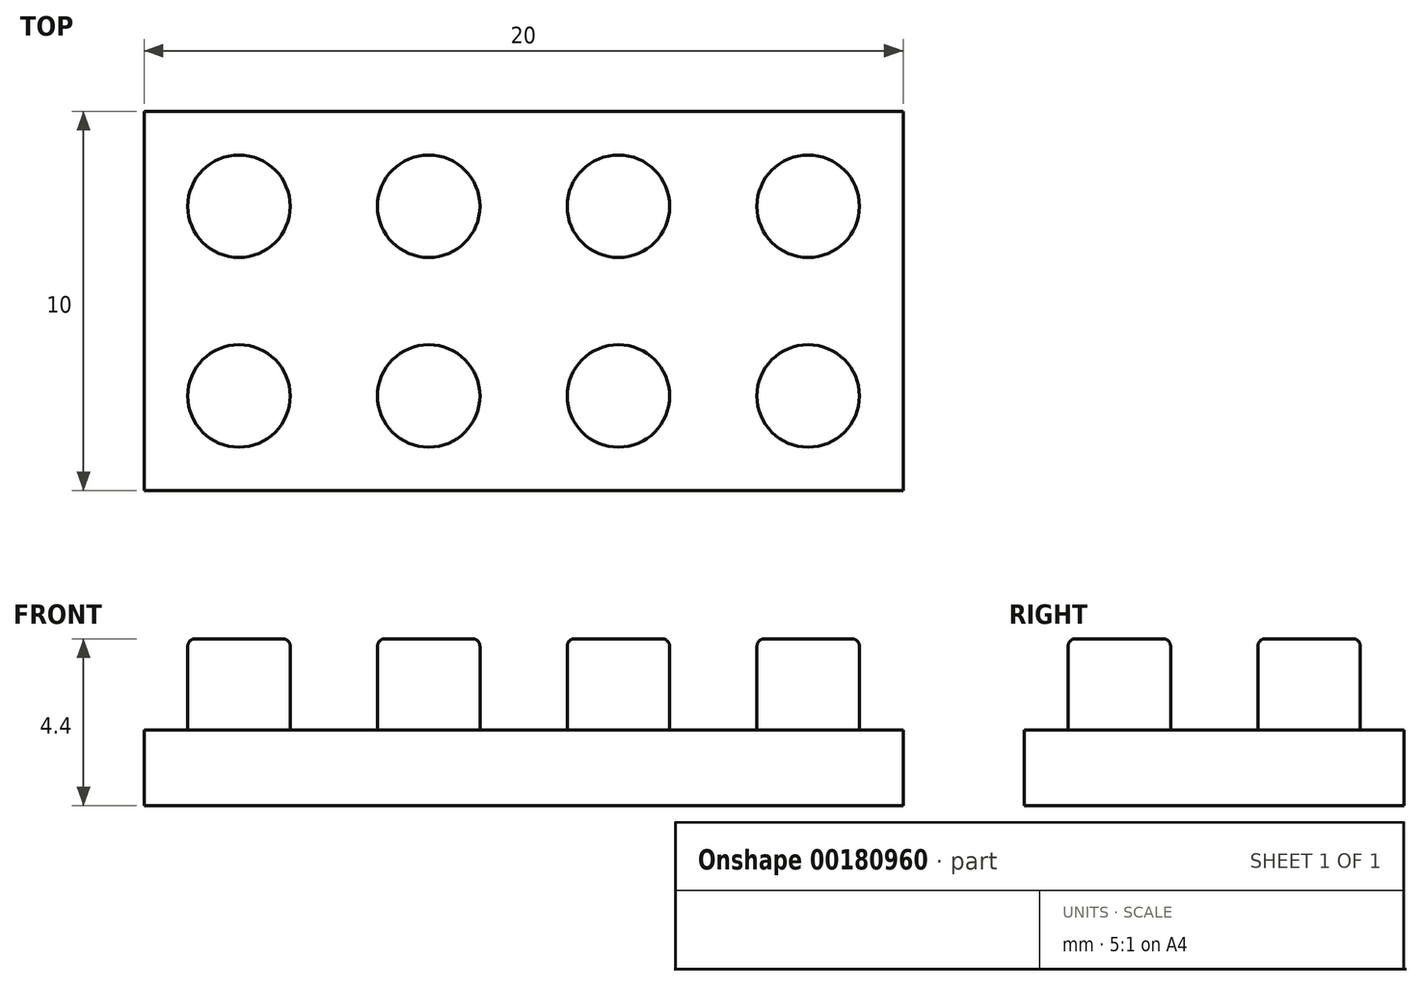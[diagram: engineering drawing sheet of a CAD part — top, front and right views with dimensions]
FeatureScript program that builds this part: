
annotation { "Feature Type Name" : "Feature", "Feature Type Description" : "" }
export const myFeature = defineFeature(function(context is Context, id is Id, definition is map)
    precondition{}
    {
        {
            var Q0;
            Q0=qCreatedBy(makeId("Top.planeOp"),FACE);
            var sketch = newSketch(context, id + "F0", { "sketchPlane" : qUnion([Q0])});
            skCircle(sketch, "E0", {"center": v(0, 0) * mm, "radius": 1.35 * mm});
            skCircle(sketch, "E1.0.1.0", {"center": v(0, 5) * mm, "radius": 1.35 * mm});
            skCircle(sketch, "E1.1.0.0", {"center": v(5, 0) * mm, "radius": 1.35 * mm});
            skCircle(sketch, "E1.1.1.0", {"center": v(5, 5) * mm, "radius": 1.35 * mm});
            skCircle(sketch, "E1.2.0.0", {"center": v(10, 0) * mm, "radius": 1.35 * mm});
            skCircle(sketch, "E1.2.1.0", {"center": v(10, 5) * mm, "radius": 1.35 * mm});
            skCircle(sketch, "E1.3.0.0", {"center": v(15, 0) * mm, "radius": 1.35 * mm});
            skCircle(sketch, "E1.3.1.0", {"center": v(15, 5) * mm, "radius": 1.35 * mm});
            skLineSegment(sketch, "E1.direction1", {"start": v(0, 0) * mm, "end": v(5, 0) * mm, "construction": true});
            skLineSegment(sketch, "E1.direction2", {"start": v(0, 0) * mm, "end": v(0, 5) * mm, "construction": true});
            skSolve(sketch);
        }
        {
            var Q0;
            Q0 = qSketchRegion(id + "F0", true);
            extrude(context, id + "F1", {"entities" : qUnion([Q0]), "depth" : 2.4 * mm});
        }
        {
            var Q0;
            Q0=qCreatedBy(makeId("Top.planeOp"),FACE);
            var sketch = newSketch(context, id + "F2", { "sketchPlane" : qUnion([Q0])});
            skLineSegment(sketch, "E2.bottom", {"start": v(-2.5, -2.5) * mm, "end": v(17.5, -2.5) * mm});
            skLineSegment(sketch, "E2.top", {"start": v(-2.5, 7.5) * mm, "end": v(17.5, 7.5) * mm});
            skLineSegment(sketch, "E2.left", {"start": v(-2.5, -2.5) * mm, "end": v(-2.5, 7.5) * mm});
            skLineSegment(sketch, "E2.right", {"start": v(17.5, -2.5) * mm, "end": v(17.5, 7.5) * mm});
            skPoint(sketch, "E3", {"position": v(15, 5) * mm});
            skSolve(sketch);
        }
        {
            var Q0;
            Q0 = qSketchRegion(id + "F2", true);
            extrude(context, id + "F3", {"entities" : qUnion([Q0]), "operationType" : NewBodyOperationType.ADD, "oppositeDirection" : true, "depth" : 2 * mm});
        }
        {
            var Q0;
            Q0=makeQuery(id+"F1.opExtrude","CAP_FACE",FACE,{"disambiguationData":[OSD([sQuery(id+"F0.wireOp",EDGE,"E1.0.1.0")])],"isStart":false});
            var Q1;
            Q1=makeQuery(id+"F1.opExtrude","CAP_FACE",FACE,{"disambiguationData":[OSD([sQuery(id+"F0.wireOp",EDGE,"E1.1.1.0")])],"isStart":false});
            var Q2;
            Q2=makeQuery(id+"F1.opExtrude","CAP_FACE",FACE,{"disambiguationData":[OSD([sQuery(id+"F0.wireOp",EDGE,"E1.2.1.0")])],"isStart":false});
            var Q3;
            Q3=makeQuery(id+"F1.opExtrude","CAP_FACE",FACE,{"disambiguationData":[OSD([sQuery(id+"F0.wireOp",EDGE,"E1.3.1.0")])],"isStart":false});
            var Q4;
            Q4=makeQuery(id+"F1.opExtrude","CAP_FACE",FACE,{"disambiguationData":[OSD([sQuery(id+"F0.wireOp",EDGE,"E1.3.0.0")])],"isStart":false});
            var Q5;
            Q5=makeQuery(id+"F1.opExtrude","CAP_FACE",FACE,{"disambiguationData":[OSD([sQuery(id+"F0.wireOp",EDGE,"E1.2.0.0")])],"isStart":false});
            var Q6;
            Q6=makeQuery(id+"F1.opExtrude","CAP_FACE",FACE,{"disambiguationData":[OSD([sQuery(id+"F0.wireOp",EDGE,"E1.1.0.0")])],"isStart":false});
            var Q7;
            Q7=makeQuery(id+"F1.opExtrude","CAP_FACE",FACE,{"disambiguationData":[OSD([sQuery(id+"F0.wireOp",EDGE,"E0")])],"isStart":false});
            fillet(context, id + "F4", {"entities" : qUnion([Q0, Q1, Q2, Q3, Q4, Q5, Q6, Q7]), "radius" : 0.2 * mm, "tangentPropagation" : true, "allowEdgeOverflow" : false});
        }
    });
